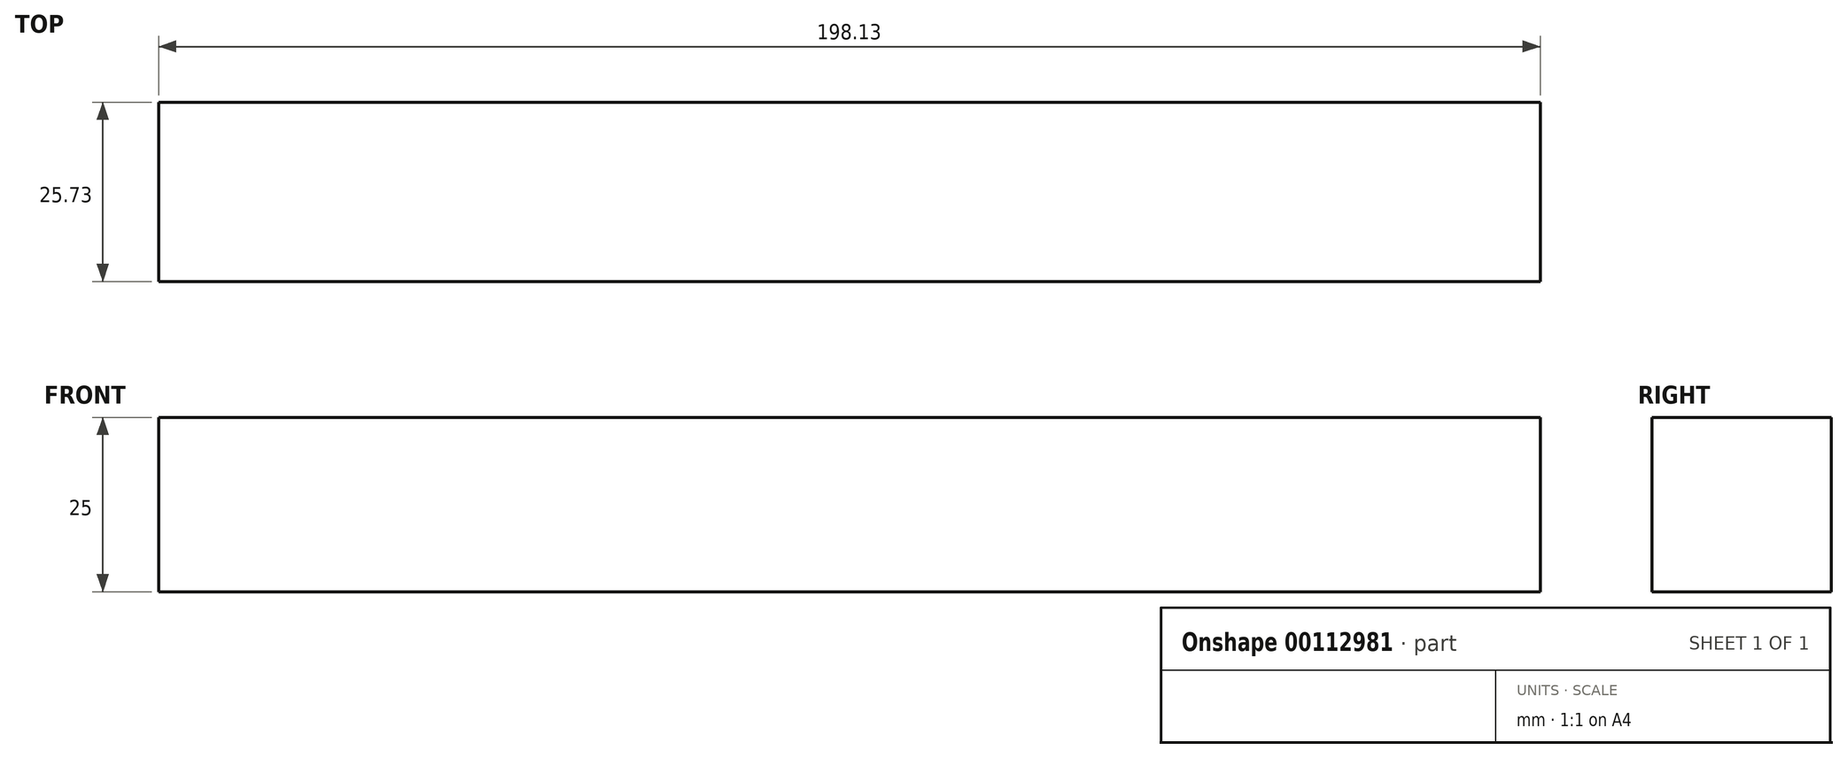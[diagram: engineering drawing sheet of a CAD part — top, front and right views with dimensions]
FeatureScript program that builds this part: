
annotation { "Feature Type Name" : "Feature", "Feature Type Description" : "" }
export const myFeature = defineFeature(function(context is Context, id is Id, definition is map)
    precondition{}
    {
        {
            var Q0;
            Q0=qCreatedBy(makeId("Top.planeOp"),FACE);
            var sketch = newSketch(context, id + "F0", { "sketchPlane" : qUnion([Q0])});
            skLineSegment(sketch, "E0.bottom", {"start": v(170.66, 42.15) * mm, "end": v(-27.47, 42.15) * mm});
            skLineSegment(sketch, "E0.top", {"start": v(170.66, 67.88) * mm, "end": v(-27.47, 67.88) * mm});
            skLineSegment(sketch, "E0.left", {"start": v(170.66, 42.15) * mm, "end": v(170.66, 67.88) * mm});
            skLineSegment(sketch, "E0.right", {"start": v(-27.47, 42.15) * mm, "end": v(-27.47, 67.88) * mm});
            skSolve(sketch);
        }
        {
            var Q0;
            Q0=makeQuery(id+"F0.imprint","IMPRINT",FACE,{"disambiguationData":[TD([[makeQuery(id+"F0.imprint","IMPRINT",EDGE,{"derivedFrom":sQuery(id+"F0.wireOp",EDGE,"E0.bottom")}),-1.0]])]});
            extrude(context, id + "F1", {"entities" : qUnion([Q0]), "depth" : 25 * mm});
        }
    });
